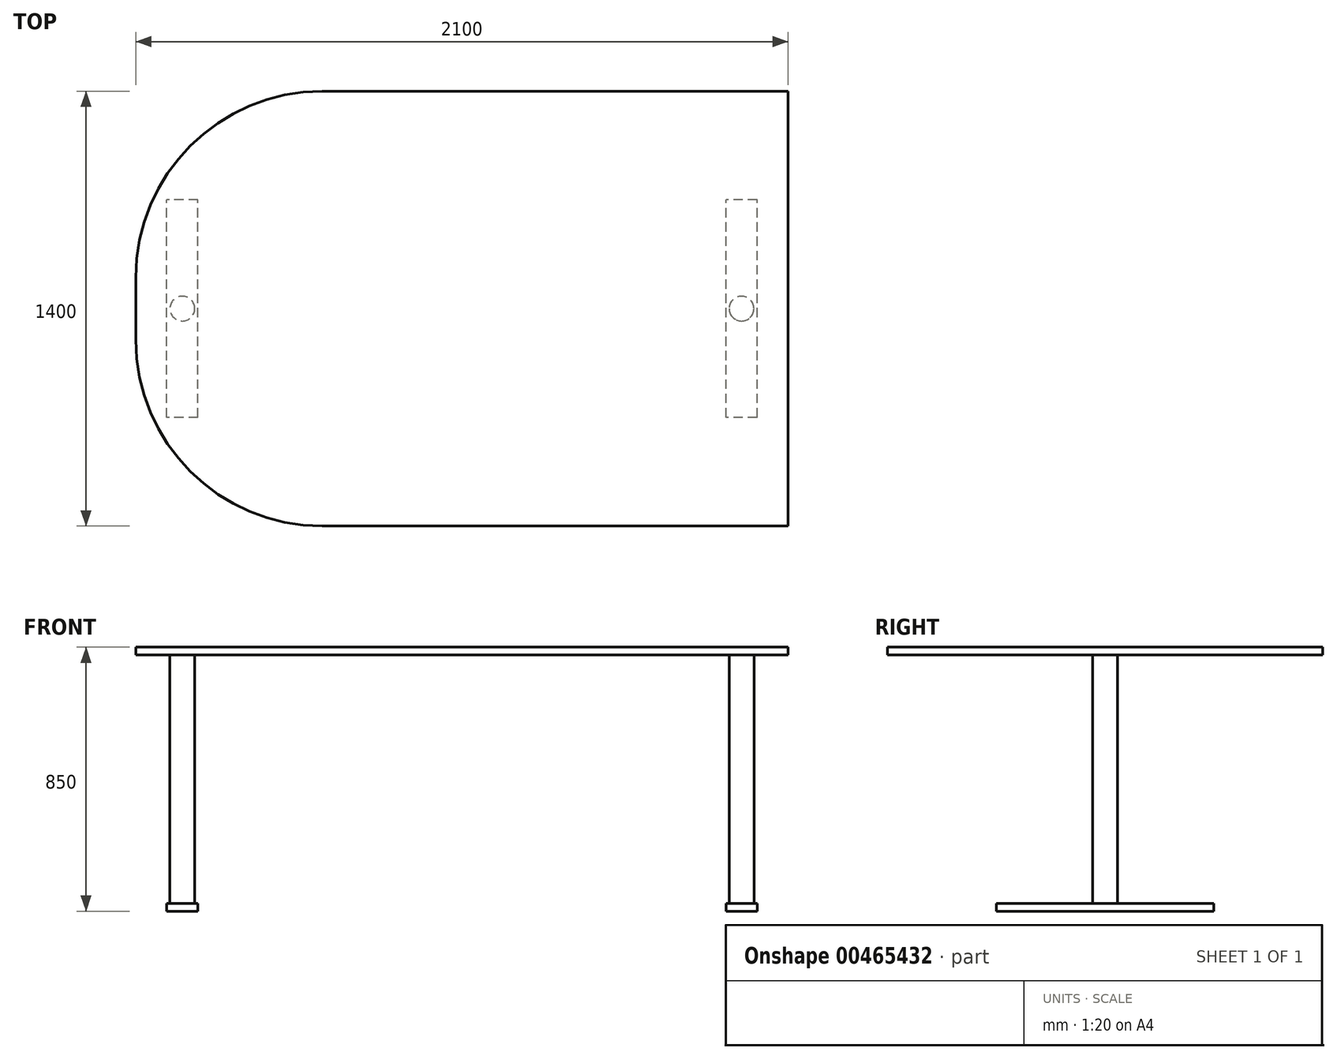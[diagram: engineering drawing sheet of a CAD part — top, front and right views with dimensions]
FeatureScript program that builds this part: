
annotation { "Feature Type Name" : "Feature", "Feature Type Description" : "" }
export const myFeature = defineFeature(function(context is Context, id is Id, definition is map)
    precondition{}
    {
        {
            var Q0;
            Q0=qCreatedBy(makeId("Top.planeOp"),FACE);
            var sketch = newSketch(context, id + "F0", { "sketchPlane" : qUnion([Q0])});
            skLineSegment(sketch, "E0.bottom", {"start": v(0, 0) * mm, "end": v(2100, 0) * mm});
            skLineSegment(sketch, "E0.top", {"start": v(0, 1400) * mm, "end": v(2100, 1400) * mm});
            skLineSegment(sketch, "E0.left", {"start": v(0, 0) * mm, "end": v(0, 1400) * mm});
            skLineSegment(sketch, "E0.right", {"start": v(2100, 0) * mm, "end": v(2100, 1400) * mm});
            skSolve(sketch);
        }
        {
            var Q0;
            Q0=qSketchRegion(id+"F0",true);
            extrude(context, id + "F1", {"entities" : qUnion([Q0]), "depth" : 25 * mm});
        }
        {
            var Q0;
            Q0=makeQuery(id+"F1.opExtrude","CAP_FACE",FACE,{"disambiguationData":[OSD([sQuery(id+"F0.wireOp",EDGE,"E0.bottom"),sQuery(id+"F0.wireOp",EDGE,"E0.top"),sQuery(id+"F0.wireOp",EDGE,"E0.left"),sQuery(id+"F0.wireOp",EDGE,"E0.right")])],"isStart":true});
            var sketch = newSketch(context, id + "F2", { "sketchPlane" : qUnion([Q0])});
            skCircle(sketch, "E1", {"center": v(150, -700) * mm, "radius": 40 * mm});
            skPoint(sketch, "E1.centerSnap0", {"position": v(0, -700) * mm});
            skCircle(sketch, "E2", {"center": v(1950, -700) * mm, "radius": 40 * mm});
            skPoint(sketch, "E2.centerSnap0", {"position": v(2100, -700) * mm});
            skSolve(sketch);
        }
        {
            var Q0;
            Q0=qSketchRegion(id+"F2",true);
            extrude(context, id + "F3", {"entities" : qUnion([Q0]), "operationType" : NewBodyOperationType.ADD, "depth" : 800 * mm});
        }
        {
            var Q0;
            Q0=makeQuery(id+"F3.opExtrude","CAP_FACE",FACE,{"disambiguationData":[OSD([sQuery(id+"F2.wireOp",EDGE,"E1")])],"isStart":false});
            var sketch = newSketch(context, id + "F4", { "sketchPlane" : qUnion([Q0])});
            skLineSegment(sketch, "E3.bottom", {"start": v(200, -350) * mm, "end": v(100, -350) * mm});
            skLineSegment(sketch, "E3.top", {"start": v(200, -1050) * mm, "end": v(100, -1050) * mm});
            skLineSegment(sketch, "E3.left", {"start": v(200, -350) * mm, "end": v(200, -1050) * mm});
            skLineSegment(sketch, "E3.right", {"start": v(100, -350) * mm, "end": v(100, -1050) * mm});
            skPoint(sketch, "E3.middle", {"position": v(150, -700) * mm});
            skSolve(sketch);
        }
        {
            var Q0;
            Q0=qSketchRegion(id+"F4",true);
            extrude(context, id + "F5", {"entities" : qUnion([Q0]), "operationType" : NewBodyOperationType.ADD, "depth" : 25 * mm});
        }
        {
            var Q0;
            Q0=makeQuery(id+"F3.opExtrude","CAP_FACE",FACE,{"disambiguationData":[OSD([sQuery(id+"F2.wireOp",EDGE,"E2")])],"isStart":false});
            var sketch = newSketch(context, id + "F6", { "sketchPlane" : qUnion([Q0])});
            skLineSegment(sketch, "E4.bottom", {"start": v(2000, -350) * mm, "end": v(1900, -350) * mm});
            skLineSegment(sketch, "E4.top", {"start": v(2000, -1050) * mm, "end": v(1900, -1050) * mm});
            skLineSegment(sketch, "E4.left", {"start": v(2000, -350) * mm, "end": v(2000, -1050) * mm});
            skLineSegment(sketch, "E4.right", {"start": v(1900, -350) * mm, "end": v(1900, -1050) * mm});
            skPoint(sketch, "E4.middle", {"position": v(1950, -700) * mm});
            skSolve(sketch);
        }
        {
            var Q0;
            Q0=qSketchRegion(id+"F6",true);
            extrude(context, id + "F7", {"entities" : qUnion([Q0]), "operationType" : NewBodyOperationType.ADD, "depth" : 25 * mm});
        }
        {
            var Q0;
            Q0=makeQuery(id+"F1.opExtrude","SWEPT_EDGE",EDGE,{"disambiguationData":[OSD([sQuery(id+"F0.wireOp",EDGE,"E0.bottom"),sQuery(id+"F0.wireOp",EDGE,"E0.left")])]});
            var Q1;
            Q1=makeQuery(id+"F1.opExtrude","SWEPT_EDGE",EDGE,{"disambiguationData":[OSD([sQuery(id+"F0.wireOp",EDGE,"E0.top"),sQuery(id+"F0.wireOp",EDGE,"E0.left")])]});
            fillet(context, id + "F8", {"entities" : qUnion([Q0, Q1]), "radius" : 600 * mm, "tangentPropagation" : true, "defaultsChanged" : false, "allowEdgeOverflow" : false, "vertexSettings" : []});
        }
        {
            var Q0;
            Q0=makeQuery(id+"F1.opExtrude","SWEPT_BODY",BODY,{"disambiguationData":[OSD([sQuery(id+"F0.wireOp",EDGE,"E0.bottom"),sQuery(id+"F0.wireOp",EDGE,"E0.top"),sQuery(id+"F0.wireOp",EDGE,"E0.left"),sQuery(id+"F0.wireOp",EDGE,"E0.right")])]});
            transform(context, id + "F9", {"entities" : qUnion([Q0]), "transformType" : TransformType.TRANSLATION_3D, "dx" : 0 * mm, "dy" : 0 * mm, "dz" : 0 * mm, "makeCopy" : true});
        }
        {
            var Q0;
            Q0=makeQuery(id+"F1.opExtrude","SWEPT_BODY",BODY,{"disambiguationData":[OSD([sQuery(id+"F0.wireOp",EDGE,"E0.bottom"),sQuery(id+"F0.wireOp",EDGE,"E0.top"),sQuery(id+"F0.wireOp",EDGE,"E0.left"),sQuery(id+"F0.wireOp",EDGE,"E0.right")])]});
            deleteBodies(context, id + "F10", {"entities" : qUnion([Q0])});
        }
    });
